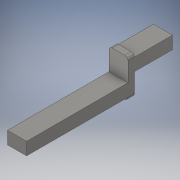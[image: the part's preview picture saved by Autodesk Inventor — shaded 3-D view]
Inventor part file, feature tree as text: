
AUTODESK INVENTOR PART (.ipt)
format: ipt  version: 2018 (Build 220112000, 112)  size: 218,624 bytes
history: native  units: in
note: dims shown in document units (in); Inventor stores cm internally (conversion verified against a paired STEP export)
features: extrude x5, sketch x5, fillet x1
ambient origin geometry x8: Origin, YZ Plane, XZ Plane, XY Plane, X Axis, Y Axis, Z Axis, Center Point
bodies: Solid1 (feature_tree)
feature tree (11):
  extrude  "Extrusion1"  Depth=2.875in
  extrude  "Extrusion2"  Depth=2.0in
  extrude  "Extrusion3"  Depth=0.375in TaperAngle=0.0deg
  extrude  "Extrusion4"  Depth=0.3125in
  extrude  "Extrusion5"  Depth=2.0in
  fillet  "Fillet1"  Radius=0.0625in
  sketch  "Sketch1"  dims[d0=0.75in d1=2.875in]
  sketch  "Sketch2"  dims[d2=0.375in d3=0.0in d4=2.0in]
  sketch  "Sketch3"  dims[d6=0.3125in d7=0.375in d8=0.0in]
  sketch  "Sketch4"  dims[d9=0.125in d10=0.3125in]
  sketch  "Sketch5"  dims[d11=0.375in d12=0.0in d13=2.0in d14=0.0625in d15=0.375in d16=0.0in d17=0.75in d18=0.0625in d19=0.375in d20=0.0in d31=0.0625in]
